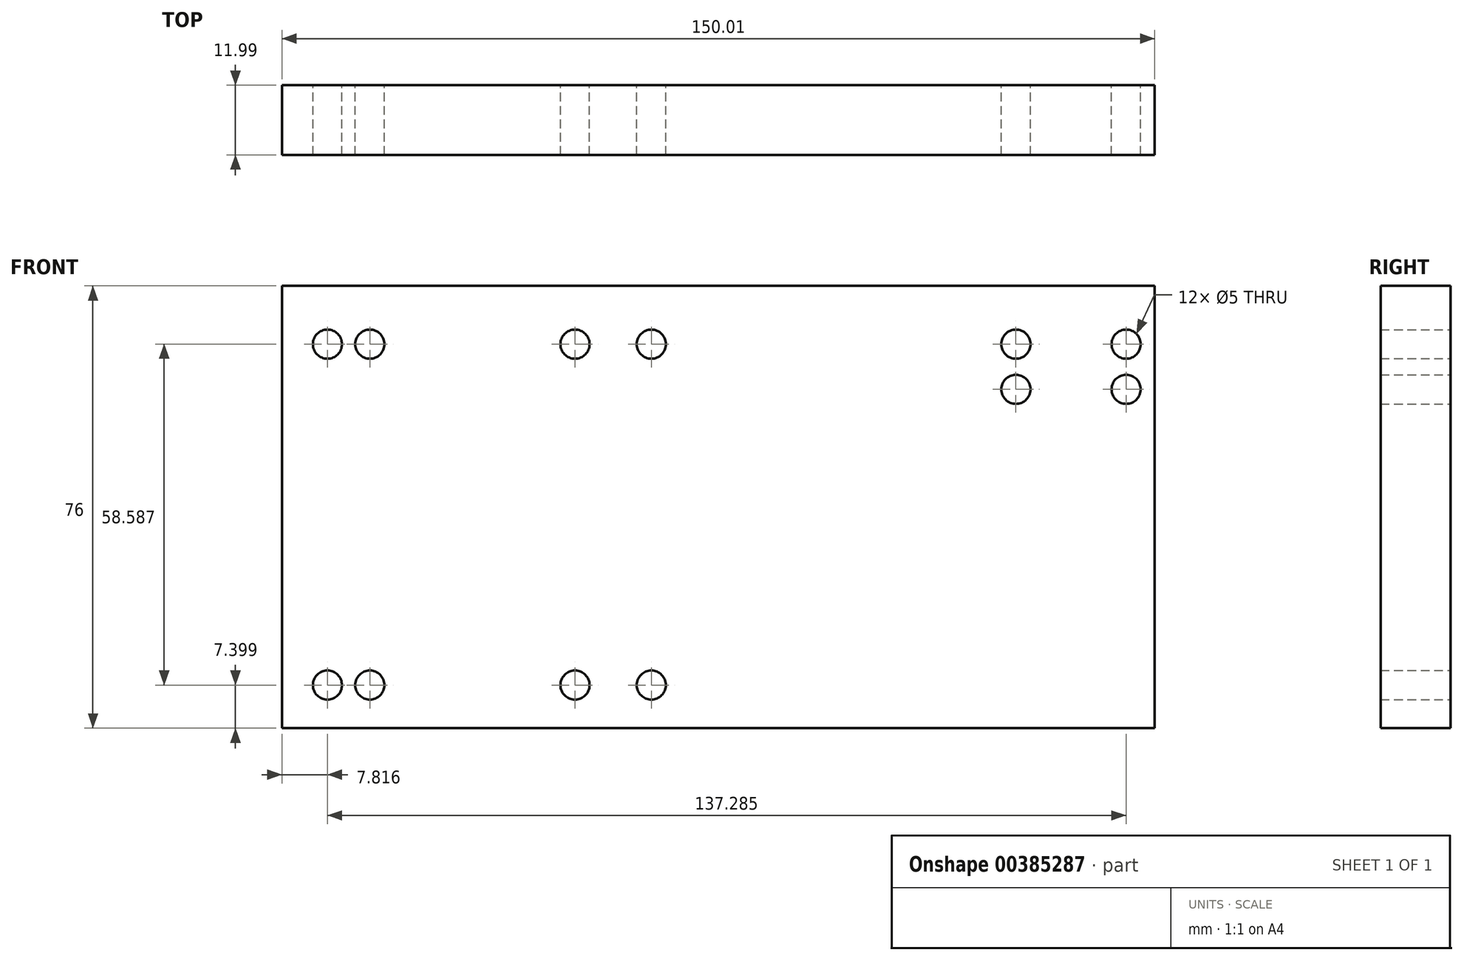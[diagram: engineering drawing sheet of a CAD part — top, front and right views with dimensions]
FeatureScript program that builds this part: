
annotation { "Feature Type Name" : "Feature", "Feature Type Description" : "" }
export const myFeature = defineFeature(function(context is Context, id is Id, definition is map)
    precondition{}
    {
        {
            var Q0;
            Q0=qCreatedBy(makeId("Front.planeOp"),FACE);
            var sketch = newSketch(context, id + "F0", { "sketchPlane" : qUnion([Q0])});
            skLineSegment(sketch, "E0.bottom", {"start": v(-75.73, 45.72) * mm, "end": v(74.28, 45.72) * mm});
            skLineSegment(sketch, "E0.top", {"start": v(-75.73, -30.28) * mm, "end": v(74.28, -30.28) * mm});
            skLineSegment(sketch, "E0.left", {"start": v(-75.73, 45.72) * mm, "end": v(-75.73, -30.28) * mm});
            skLineSegment(sketch, "E0.right", {"start": v(74.28, 45.72) * mm, "end": v(74.28, -30.28) * mm});
            skCircle(sketch, "E1", {"center": v(-67.91, 35.7) * mm, "radius": 2.5 * mm});
            skCircle(sketch, "E2", {"center": v(-60.63, 35.7) * mm, "radius": 2.5 * mm});
            skCircle(sketch, "E3", {"center": v(-25.36, 35.7) * mm, "radius": 2.5 * mm});
            skCircle(sketch, "E4", {"center": v(-12.24, 35.7) * mm, "radius": 2.5 * mm});
            skCircle(sketch, "E5", {"center": v(50.43, 35.7) * mm, "radius": 2.5 * mm});
            skCircle(sketch, "E6", {"center": v(69.37, 35.7) * mm, "radius": 2.5 * mm});
            skCircle(sketch, "E7", {"center": v(-67.91, -22.88) * mm, "radius": 2.5 * mm});
            skCircle(sketch, "E8", {"center": v(-60.63, -22.88) * mm, "radius": 2.5 * mm});
            skCircle(sketch, "E9", {"center": v(-25.36, -22.88) * mm, "radius": 2.5 * mm});
            skCircle(sketch, "E10", {"center": v(-12.24, -22.88) * mm, "radius": 2.5 * mm});
            skCircle(sketch, "E11", {"center": v(50.43, 27.94) * mm, "radius": 2.5 * mm});
            skCircle(sketch, "E12", {"center": v(69.37, 27.94) * mm, "radius": 2.5 * mm});
            skSolve(sketch);
        }
        {
            var Q0;
            Q0=makeQuery(id+"F0.imprint","IMPRINT",FACE,{"disambiguationData":[TD([[makeQuery(id+"F0.imprint","IMPRINT",EDGE,{"derivedFrom":sQuery(id+"F0.wireOp",EDGE,"E0.bottom")}),-1.0]])]});
            extrude(context, id + "F1", {"entities" : qUnion([Q0]), "depth" : 12 * mm});
        }
    });
